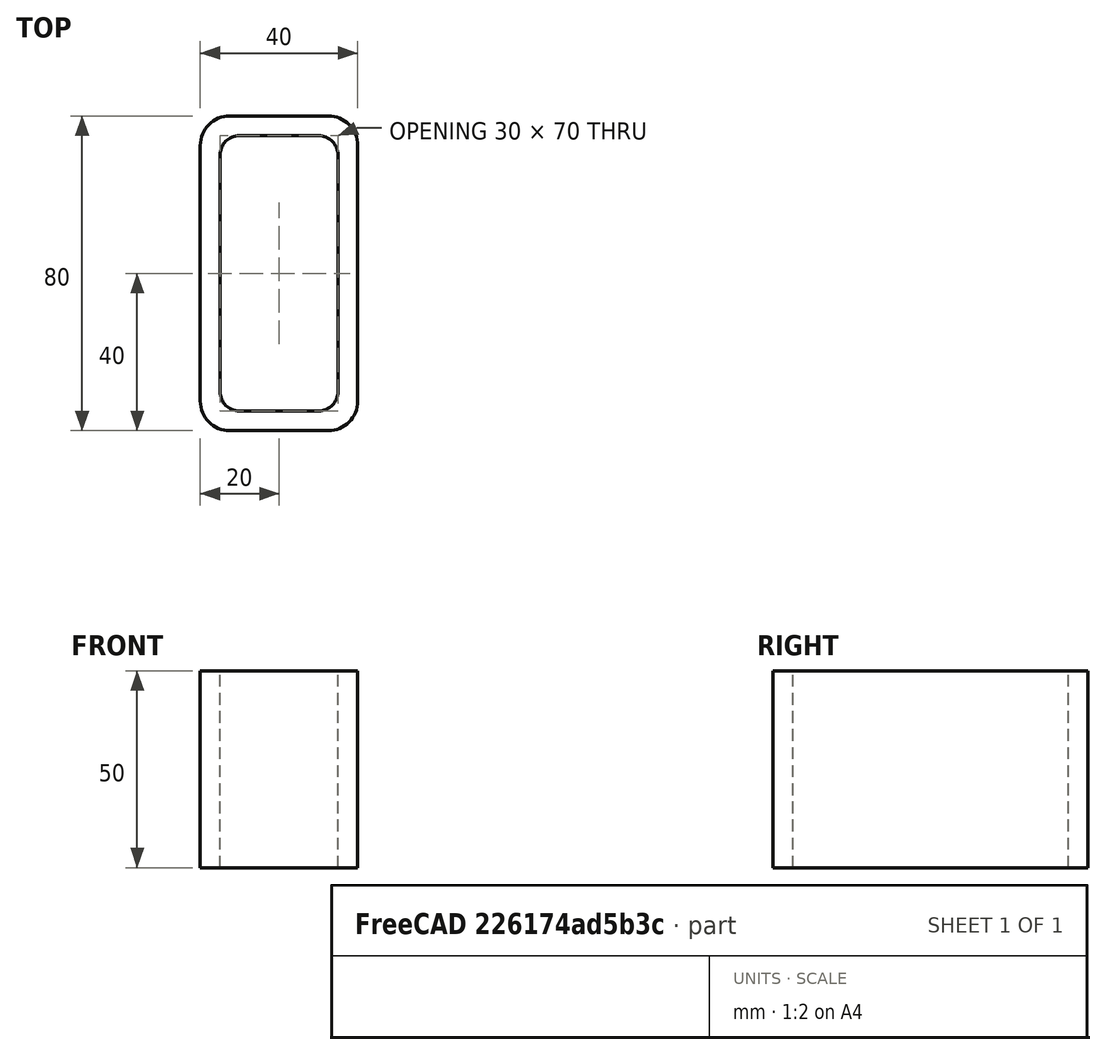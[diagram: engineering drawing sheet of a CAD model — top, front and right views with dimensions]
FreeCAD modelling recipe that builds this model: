
FCSTD DOCUMENT  (FreeCAD 0.15R4671 (Git))
Label: Rectangular hollow section 80x40x5 EN10219 S235JRH
License: All rights reserved
LicenseURL: http://en.wikipedia.org/wiki/All_rights_reserved
objects: Sketcher::SketchObject×1, Part::Extrusion×1
note: 2 computed .brp shape members not serialized (recipe doc carries the construction recipe); baked Part::Feature solids carry a one-line shape summary decoded from their .brp

FEATURE [Sketcher::SketchObject] Sketch
  sketch-geometry (16):
    g0: LineSegment StartX=-10 StartY=35 StartZ=0 EndX=10 EndY=35 EndZ=0
    g1: LineSegment StartX=15 StartY=30 StartZ=0 EndX=15 EndY=-30 EndZ=0
    g2: LineSegment StartX=10 StartY=-35 StartZ=0 EndX=-10 EndY=-35 EndZ=0
    g3: LineSegment StartX=-15 StartY=-30 StartZ=0 EndX=-15 EndY=30 EndZ=0
    g4: LineSegment StartX=-12.5 StartY=40 StartZ=0 EndX=12.5 EndY=40 EndZ=0
    g5: LineSegment StartX=20 StartY=32.5 StartZ=0 EndX=20 EndY=-32.5 EndZ=0
    g6: LineSegment StartX=12.5 StartY=-40 StartZ=0 EndX=-12.5 EndY=-40 EndZ=0
    g7: LineSegment StartX=-20 StartY=-32.5 StartZ=0 EndX=-20 EndY=32.5 EndZ=0
    g8: ArcOfCircle CenterX=-10 CenterY=30 CenterZ=0 NormalX=0 NormalY=0 NormalZ=1 Radius=5 StartAngle=1.5708 EndAngle=3.14159
    g9: ArcOfCircle CenterX=10 CenterY=30 CenterZ=0 NormalX=0 NormalY=0 NormalZ=1 Radius=5 StartAngle=0 EndAngle=1.5708
    g10: ArcOfCircle CenterX=10 CenterY=-30 CenterZ=0 NormalX=0 NormalY=0 NormalZ=1 Radius=5 StartAngle=4.71239 EndAngle=6.28319
    g11: ArcOfCircle CenterX=-10 CenterY=-30 CenterZ=0 NormalX=0 NormalY=0 NormalZ=1 Radius=5 StartAngle=3.14159 EndAngle=4.71239
    g12: ArcOfCircle CenterX=12.5 CenterY=32.5 CenterZ=0 NormalX=0 NormalY=0 NormalZ=1 Radius=7.5 StartAngle=0 EndAngle=1.5708
    g13: ArcOfCircle CenterX=12.5 CenterY=-32.5 CenterZ=0 NormalX=0 NormalY=0 NormalZ=1 Radius=7.5 StartAngle=4.71239 EndAngle=6.28319
    g14: ArcOfCircle CenterX=-12.5 CenterY=-32.5 CenterZ=0 NormalX=0 NormalY=0 NormalZ=1 Radius=7.5 StartAngle=3.14159 EndAngle=4.71239
    g15: ArcOfCircle CenterX=-12.5 CenterY=32.5 CenterZ=0 NormalX=0 NormalY=0 NormalZ=1 Radius=7.5 StartAngle=1.5708 EndAngle=3.14159
  constraints (36):
    c: Horizontal(g2)
    c: Vertical(g3)
    c: Horizontal(g6)
    c: Vertical(g7)
    c: Tangent(g3,g8) = 1.5708
    c: Tangent(g0,g8) = 1.5708
    c: Tangent(g0,g9) = 1.5708
    c: Tangent(g1,g9) = 1.5708
    c: Tangent(g1,g10) = 1.5708
    c: Tangent(g2,g10) = 1.5708
    c: Tangent(g2,g11) = 1.5708
    c: Tangent(g3,g11) = 1.5708
    c: Tangent(g4,g12) = 1.5708
    c: Tangent(g5,g12) = 1.5708
    c: Tangent(g5,g13) = 1.5708
    c: Tangent(g6,g13) = 1.5708
    c: Tangent(g6,g14) = 1.5708
    c: Tangent(g7,g14) = 1.5708
    c: Tangent(g7,g15) = 1.5708
    c: Tangent(g4,g15) = 1.5708
    c: Equal(g9,g8)
    c: Equal(g9,g11)
    c: Equal(g9,g10)
    c: Equal(g12,g15)
    c: Equal(g12,g14)
    c: Equal(g12,g13)
    c: Symmetric(g4,g6,g-1)
    c: Symmetric(g7,g5,g-2)
    c: DistanceY(g4,g6) = -80
    c: DistanceX(g7,g5) = 40
    c: Symmetric(g3,g1,g-2)
    c: Symmetric(g0,g2,g-1)
    c: DistanceY(g0,g4) = 5
    c: DistanceX(g5,g1) = -5
    c: Radius(g9) = 5
    c: Radius(g12) = 7.5
FEATURE [Part::Extrusion] Extrude  label="Rectangular hollow section 80x40x5 EN10219 S235JRH"
  Base = -> Sketch
  Dir = (0,0,50)
  Solid = true
